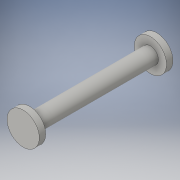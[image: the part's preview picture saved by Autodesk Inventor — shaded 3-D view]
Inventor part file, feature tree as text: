
AUTODESK INVENTOR PART (.ipt)
format: ipt  version: 2016 (Build 200138000, 138)  size: 103,936 bytes
history: native  units: in
note: dims shown in document units (in); Inventor stores cm internally (conversion verified against a paired STEP export)
features: extrude x3, sketch x3
ambient origin geometry x8: Origin, YZ Plane, XZ Plane, XY Plane, X Axis, Y Axis, Z Axis, Center Point
bodies: Solid1 (feature_tree)
feature tree (6):
  extrude  "Extrusion1"  Depth=0.375in TaperAngle=0.0deg
  extrude  "Extrusion2"  Depth=0.02in TaperAngle=0.0deg
  extrude  "Extrusion3"  [1 undecoded]
  sketch  "Sketch1"  dims[d0=0.05in d1=0.375in d2=0.0in]
  sketch  "Sketch2"  dims[d3=0.1in d4=0.02in d5=0.0in]
  sketch  "Sketch3"  dims[d6=0.02in d7=0.0in]
note: 1 required parameter value undecoded (feature->parameter linkage not recoverable at this tier; creation-order binding heuristic only, values carry confidence <= 0.55)
